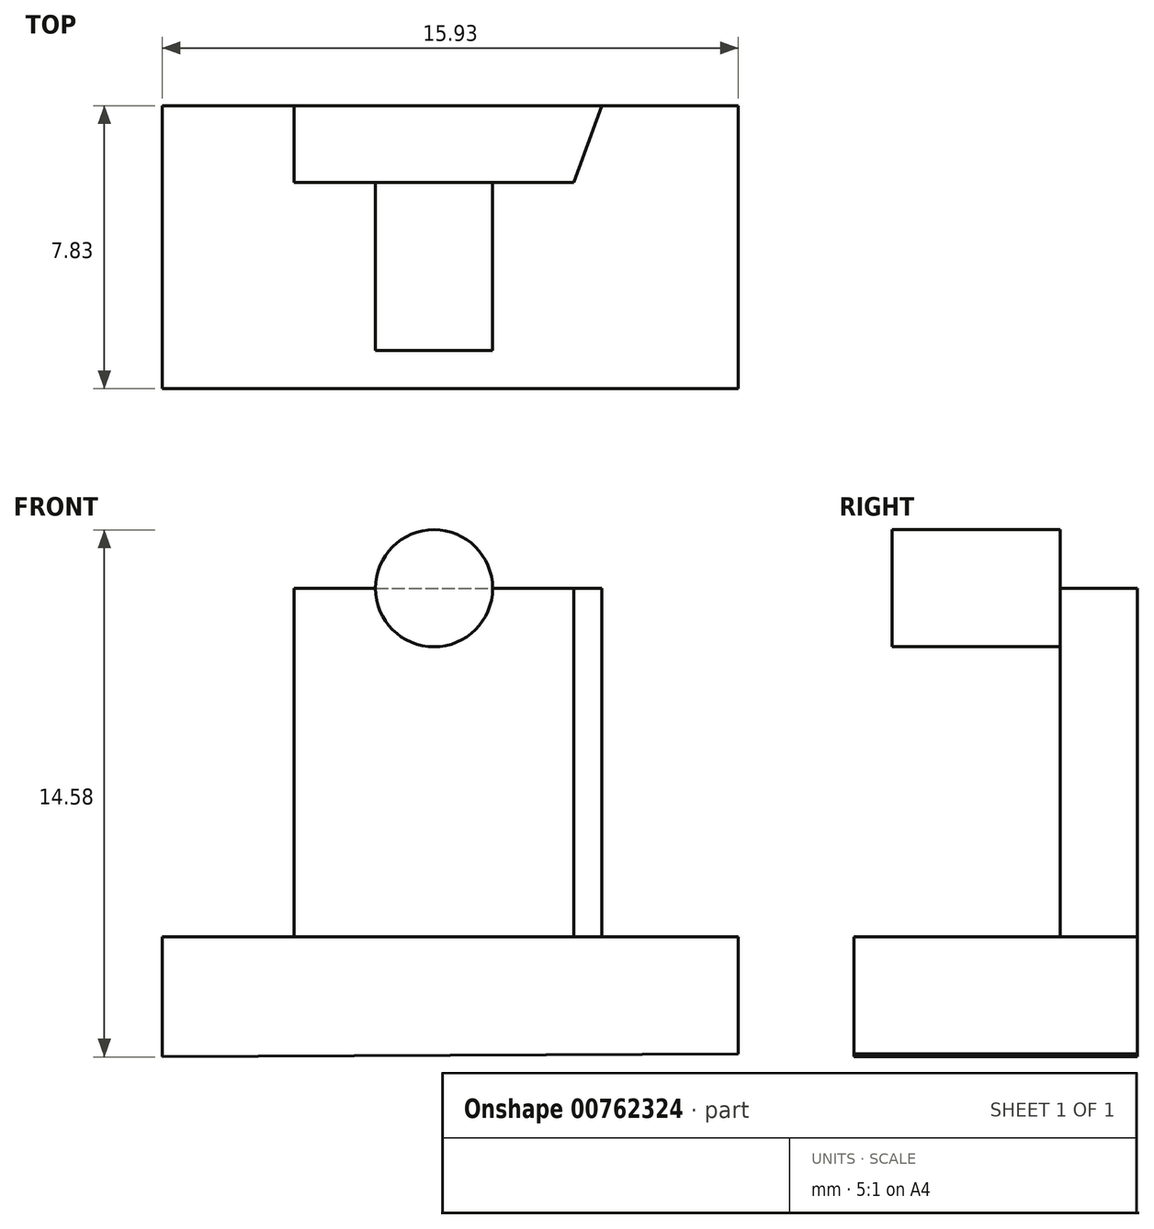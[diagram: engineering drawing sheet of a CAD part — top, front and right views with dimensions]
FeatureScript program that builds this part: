
annotation { "Feature Type Name" : "Feature", "Feature Type Description" : "" }
export const myFeature = defineFeature(function(context is Context, id is Id, definition is map)
    precondition{}
    {
        {
            var Q0;
            Q0=qCreatedBy(makeId("Front.planeOp"),FACE);
            var sketch = newSketch(context, id + "F0", { "sketchPlane" : qUnion([Q0])});
            skLineSegment(sketch, "E0", {"start": v(-51.95, -28.85) * mm, "end": v(-51.95, -32.17) * mm});
            skLineSegment(sketch, "E1", {"start": v(-51.95, -28.85) * mm, "end": v(-36.02, -28.85) * mm});
            skLineSegment(sketch, "E2", {"start": v(-36.02, -32.1) * mm, "end": v(-51.95, -32.17) * mm});
            skLineSegment(sketch, "E3", {"start": v(-36.02, -28.85) * mm, "end": v(-36.02, -32.1) * mm});
            skSolve(sketch);
        }
        {
            var Q0;
            Q0 = qSketchRegion(id + "F0", true);
            extrude(context, id + "F1", {"entities" : qUnion([Q0]), "depth" : 7.83 * mm, "offsetDistance" : 25 * mm});
        }
        {
            var Q0;
            Q0=makeQuery(id+"F1.opExtrude","SWEPT_FACE",FACE,{"disambiguationData":[OSD([sQuery(id+"F0.wireOp",EDGE,"E1")])]});
            var sketch = newSketch(context, id + "F2", { "sketchPlane" : qUnion([Q0])});
            skPoint(sketch, "E4.end.orphan", {"position": v(-48.3, -2.12) * mm});
            skPoint(sketch, "E4.start.orphan", {"position": v(-48.3, -4.67) * mm});
            skPoint(sketch, "E5.end.orphan", {"position": v(-40.57, -2.12) * mm});
            skPoint(sketch, "E6.start.orphan", {"position": v(-48.3, 0) * mm});
            skLineSegment(sketch, "E7", {"start": v(-48.3, 0) * mm, "end": v(-39.8, 0) * mm});
            skLineSegment(sketch, "E8", {"start": v(-48.3, -2.12) * mm, "end": v(-40.57, -2.12) * mm});
            skLineSegment(sketch, "E9", {"start": v(-48.3, 0) * mm, "end": v(-48.3, -2.12) * mm});
            skLineSegment(sketch, "E10", {"start": v(-39.8, 0) * mm, "end": v(-40.57, -2.12) * mm});
            skSolve(sketch);
        }
        {
            var Q0;
            Q0 = qSketchRegion(id + "F2", true);
            extrude(context, id + "F3", {"entities" : qUnion([Q0]), "depth" : 9.64 * mm, "offsetDistance" : 25 * mm});
        }
        {
            var Q0;
            Q0=makeQuery(id+"F3.opExtrude","SWEPT_FACE",FACE,{"disambiguationData":[OSD([sQuery(id+"F2.wireOp",EDGE,"E8")])]});
            var sketch = newSketch(context, id + "F4", { "sketchPlane" : qUnion([Q0])});
            skPoint(sketch, "E11.start.orphan", {"position": v(-40.57, -16.38) * mm});
            skPoint(sketch, "E12.endSnap0", {"position": v(-44.43, -19.2) * mm});
            skPoint(sketch, "E12.end.orphan", {"position": v(-44.43, -16.97) * mm});
            skPoint(sketch, "E13.end.orphan", {"position": v(41.24, 0) * mm});
            skPoint(sketch, "E14.start.orphan", {"position": v(-44.43, -14.34) * mm});
            skCircle(sketch, "E15", {"center": v(-44.43, -19.2) * mm, "radius": 1.62 * mm});
            skSolve(sketch);
        }
        {
            var Q0;
            Q0 = qSketchRegion(id + "F4", true);
            extrude(context, id + "F5", {"entities" : qUnion([Q0]), "operationType" : NewBodyOperationType.ADD, "depth" : 4.65 * mm, "offsetDistance" : 25 * mm});
        }
    });
